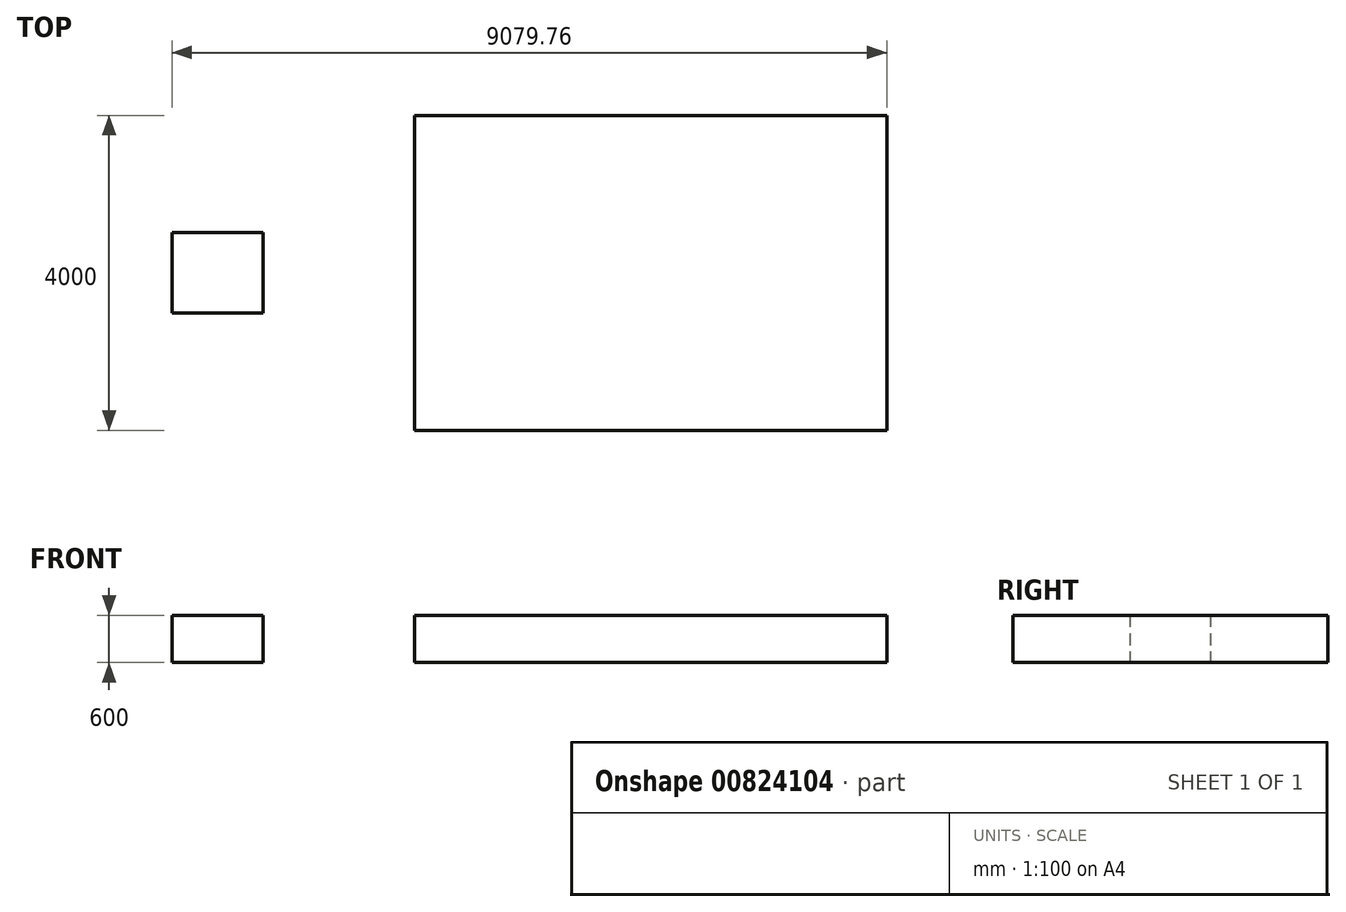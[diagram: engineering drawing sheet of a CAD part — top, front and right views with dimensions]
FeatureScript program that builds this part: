
annotation { "Feature Type Name" : "Feature", "Feature Type Description" : "" }
export const myFeature = defineFeature(function(context is Context, id is Id, definition is map)
    precondition{}
    {
        {
            var Q0;
            Q0=qCreatedBy(makeId("Top.planeOp"),FACE);
            var sketch = newSketch(context, id + "F0", { "sketchPlane" : qUnion([Q0])});
            skLineSegment(sketch, "E0.bottom", {"start": v(-3000, -2000) * mm, "end": v(3000, -2000) * mm});
            skLineSegment(sketch, "E0.top", {"start": v(-3000, 2000) * mm, "end": v(3000, 2000) * mm});
            skLineSegment(sketch, "E0.left", {"start": v(-3000, -2000) * mm, "end": v(-3000, 2000) * mm});
            skLineSegment(sketch, "E0.right", {"start": v(3000, -2000) * mm, "end": v(3000, 2000) * mm});
            skPoint(sketch, "E0.middle", {"position": v(0, 0) * mm});
            skLineSegment(sketch, "E1.bottom", {"start": v(-6079.76, -510.67) * mm, "end": v(-4925.2, -510.67) * mm});
            skLineSegment(sketch, "E1.top", {"start": v(-6079.76, 510.67) * mm, "end": v(-4925.2, 510.67) * mm});
            skLineSegment(sketch, "E1.left", {"start": v(-6079.76, -510.67) * mm, "end": v(-6079.76, 510.67) * mm});
            skLineSegment(sketch, "E1.right", {"start": v(-4925.2, -510.67) * mm, "end": v(-4925.2, 510.67) * mm});
            skPoint(sketch, "E1.middle", {"position": v(-5502.47, 0) * mm});
            skLineSegment(sketch, "E2", {"start": v(-2520.74, 1629.25) * mm, "end": v(-2520.74, 29.25) * mm});
            skLineSegment(sketch, "E3", {"start": v(-2520.74, 29.25) * mm, "end": v(-2120.74, 29.25) * mm});
            skLineSegment(sketch, "E4", {"start": v(-2120.74, 29.25) * mm, "end": v(-2120.74, 1030) * mm});
            skLineSegment(sketch, "E5", {"start": v(-2120.74, 1030) * mm, "end": v(-720.74, 1030) * mm});
            skLineSegment(sketch, "E6", {"start": v(-720.74, 1030) * mm, "end": v(-720.74, 1630) * mm});
            skLineSegment(sketch, "E7", {"start": v(-720.74, 1630) * mm, "end": v(-2520.74, 1630) * mm});
            skSolve(sketch);
        }
        {
            var Q0;
            Q0 = qSketchRegion(id + "F0", true);
            var Q1;
            Q1=sQuery(id+"F0.wireOp",EDGE,"E4");
            var Q2;
            Q2=sQuery(id+"F0.wireOp",EDGE,"E3");
            var Q3;
            Q3=sQuery(id+"F0.wireOp",EDGE,"E5");
            var Q4;
            Q4=sQuery(id+"F0.wireOp",EDGE,"E6");
            var Q5;
            Q5=sQuery(id+"F0.wireOp",EDGE,"E2");
            var Q6;
            Q6=sQuery(id+"F0.wireOp",EDGE,"E7");
            extrude(context, id + "F1", {"entities" : qUnion([Q0]), "surfaceEntities" : qUnion([Q1, Q2, Q3, Q4, Q5, Q6]), "depth" : 600 * mm, "offsetDistance" : 25 * mm});
        }
    });
